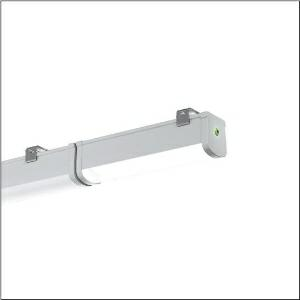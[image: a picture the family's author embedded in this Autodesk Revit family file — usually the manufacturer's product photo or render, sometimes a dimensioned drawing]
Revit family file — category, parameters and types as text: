
# Revit family: monsun_r__31_58fa207a403b3g_c1e4
name_source: partatom
category: Lighting Fixtures
units: mm (PartAtom-declared; Revit-internal decimal feet)

## family parameters
Cut with Voids When Loaded = No
Host = Face
Light Source = No
Part Type = Normal
Room Calculation Point = No
Round Connector Dimension = Use Diameter
Shared = No

## types (1)
- --- (1 x LED, 450 lm, 5 W, 4000K)
    Apparent Load = 5 VA
    CIE Flux Codes = 42 72 91 92 100
    Color Rendering = 80
    Color Temperature = 4000K
    Default Elevation = 1800 mm
    Description = Monsun® 31, emergency light element, primary optical cover: diffuser, of PC, frosted, light emission: direct distribution, primary light characteristic: symmetric, installation type: surface-mounted, EM-KIT 3h,LED, rated luminous flux: 450lm, luminous efficacy: 100lm/W, light colour: 840, colour temperature: 4000K, control gear: ON/OFF, emergency light function, with socket/plug, mains connection: 220..240V, AC, 50..60Hz, rated input power: 5W, housing, luminaire housing, of PC, light grey (RAL 7035), length: 297mm, width: 68mm, height: 76mm, protection rating (complete): IP65, insulation class (complete): insulation class II (safety insulation), certification: CE, protection symbol: D, impact resistance: IK08, permissible operating ambient temperature: 0..+40°C, standard: EN 60598-2-22, corresponds to IFS (International Featured Standards) requirements for safety and quality in the food industry, packaging unit: 1 piece
    Height = 77 mm
    Lamp = 1 x LED
    Lamp Light Flux = 450 lm
    Lamp Power = 5 W
    Lamp count = 1
    Length = 294 mm
    Luminous efficacy = 90 lm/W
    Manufacturer = Siteco
    ModVariant = No
    Model = 58FA207A403B3G
    Mounting Place = Ceiling
    Mounting Type = Surface mounted
    Number of Poles = 1
    OnlyDefault = Yes
    Power Factor = 1
    Product Name = Monsun® 31
    Product group = emergency light element
    ProductGroupID = 308
    Protection Class = Protection class II
    Protection Degree = IP 65
    RLX_Detail_Level = 1
    RLX_Emergency_Light_Flux = 0 lm
    RLX_Emergency_Type = 0
    RLX_Emergency_Type_DB = No
    RlxData = <blob elided: 31137 chars, md5=ee17babe>
    Socket = socket
    Standby Power = 0 W
    System Light Flux = 450 lm
    System Power = 5 W
    Type Comments = : 3 h
    Type Image = l_1006658.jpg
    URL = http://relux.com
    VarID = @adj_197770
    Voltage = 0 V
    Weight = 0.00 kg
    Width = 69 mm

## geometry (parser evidence)
native form markers: Blend x4, Sweep x11
no freeform markers — native parametric forms only
